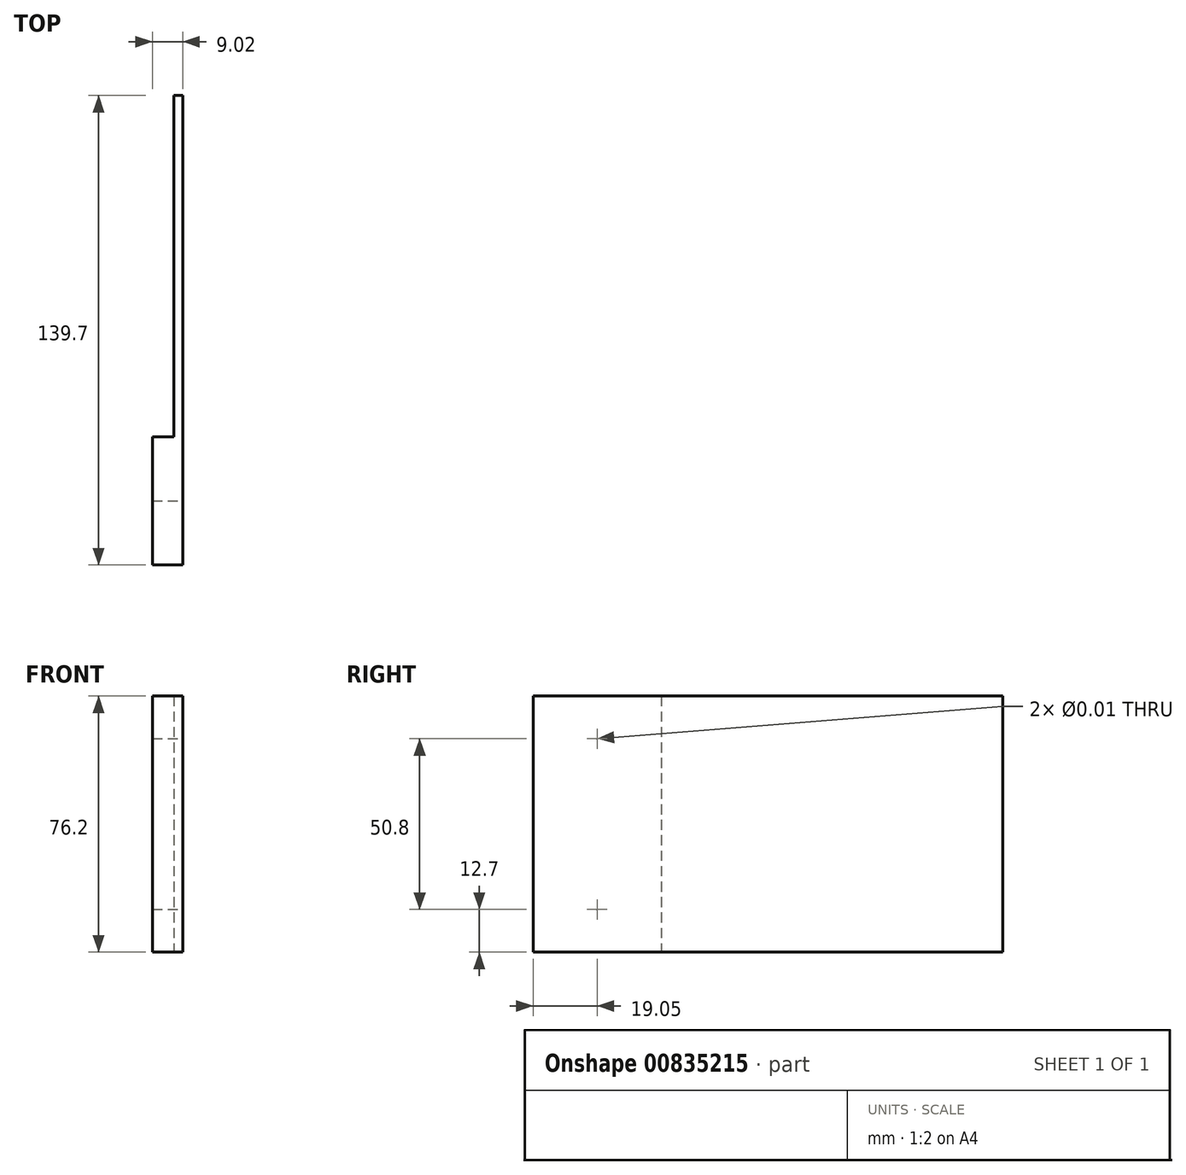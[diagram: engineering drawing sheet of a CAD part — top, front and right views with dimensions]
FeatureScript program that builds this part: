
annotation { "Feature Type Name" : "Feature", "Feature Type Description" : "" }
export const myFeature = defineFeature(function(context is Context, id is Id, definition is map)
    precondition{}
    {
        {
            var Q0;
            Q0=qCreatedBy(makeId("Top.planeOp"),FACE);
            var sketch = newSketch(context, id + "F0", { "sketchPlane" : qUnion([Q0])});
            skLineSegment(sketch, "E0", {"start": v(0, 0) * mm, "end": v(0, 38.1) * mm});
            skLineSegment(sketch, "E1", {"start": v(0, 38.1) * mm, "end": v(6.35, 38.1) * mm});
            skLineSegment(sketch, "E2", {"start": v(6.35, 38.1) * mm, "end": v(6.35, 139.7) * mm});
            skLineSegment(sketch, "E3", {"start": v(9.02, 139.7) * mm, "end": v(9.02, 0) * mm});
            skLineSegment(sketch, "E4", {"start": v(9.02, 0) * mm, "end": v(0, 0) * mm});
            skLineSegment(sketch, "E5", {"start": v(9.02, 139.7) * mm, "end": v(6.35, 139.7) * mm});
            skSolve(sketch);
        }
        {
            var Q0;
            Q0 = qSketchRegion(id + "F0", true);
            extrude(context, id + "F1", {"entities" : qUnion([Q0]), "endBound" : BoundingType.SYMMETRIC, "depth" : 76.2 * mm, "offsetDistance" : 25.4 * mm});
        }
        {
            var Q0;
            Q0=makeQuery(id+"F1.opExtrude","SWEPT_FACE",FACE,{"disambiguationData":[OSD([sQuery(id+"F0.wireOp",EDGE,"E3")])]});
            var sketch = newSketch(context, id + "F2", { "sketchPlane" : qUnion([Q0])});
            skPoint(sketch, "E6", {"position": v(19.05, 25.4) * mm});
            skPoint(sketch, "E7", {"position": v(19.05, -25.4) * mm});
            skSolve(sketch);
        }
        {
            var Q0;
            Q0=sQuery(id+"F2.wireOp",VERTEX,"E6");
            var Q1;
            Q1=sQuery(id+"F2.wireOp",VERTEX,"E7");
            var Q2;
            Q2=makeQuery(id+"F1.opExtrude","SWEPT_BODY",BODY,{"disambiguationData":[OSD([sQuery(id+"F0.wireOp",EDGE,"E0"),sQuery(id+"F0.wireOp",EDGE,"E1"),sQuery(id+"F0.wireOp",EDGE,"E2"),sQuery(id+"F0.wireOp",EDGE,"koUcHW5e-egy5-PZqg-fJgw-fYBq1sQbbxHi"),sQuery(id+"F0.wireOp",EDGE,"E3"),sQuery(id+"F0.wireOp",EDGE,"E4")])]});
            hole(context, id + "F3", {"style" : HoleStyle.SIMPLE, "endStyle" : HoleEndStyle.THROUGH, "standardTappedOrClearance" : lookupTablePath({ "standard" : "ANSI", "size" : "5/16 (0.31)", "type" : "Drilled" }), "standardBlindInLast" : lookupTablePath({ "standard" : "ANSI", "size" : "5/16", "type" : "Drilled" }), "holeDiameter" : 5 / 406.4 * mm, "majorDiameter" : 6.35 * mm, "isTappedThrough" : true, "tappedDepth" : 12.7 * mm, "tapClearance" : 3, "startFromSketch" : true, "locations" : qUnion([Q0, Q1]), "scope" : qUnion([Q2])});
        }
    });
